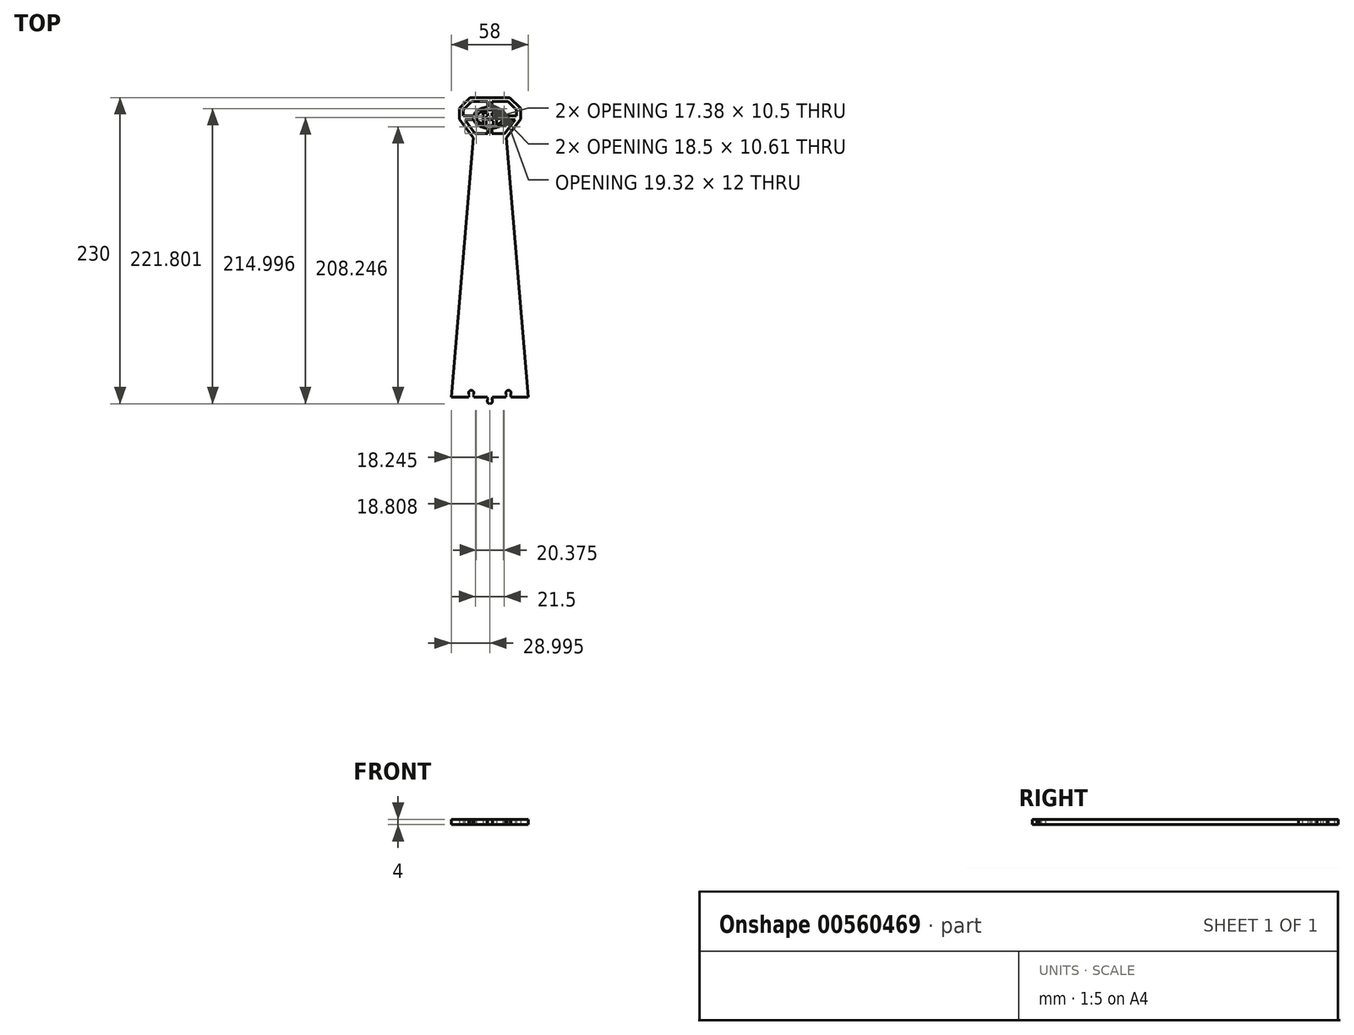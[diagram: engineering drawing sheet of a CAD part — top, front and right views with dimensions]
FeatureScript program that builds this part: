
annotation { "Feature Type Name" : "Feature", "Feature Type Description" : "" }
export const myFeature = defineFeature(function(context is Context, id is Id, definition is map)
    precondition{}
    {
        {
            var Q0;
            Q0=qCreatedBy(makeId("Top.planeOp"),FACE);
            var sketch = newSketch(context, id + "F0", { "sketchPlane" : qUnion([Q0])});
            skLineSegment(sketch, "E0.bottom", {"start": v(14.64, 150.88) * mm, "end": v(-15.36, 150.88) * mm});
            skLineSegment(sketch, "E0.top", {"start": v(12.14, 120.88) * mm, "end": v(-12.86, 120.88) * mm});
            skPoint(sketch, "E0.middle", {"position": v(-0.36, 135.88) * mm});
            skPoint(sketch, "E1", {"position": v(-0.36, 120.88) * mm});
            skPoint(sketch, "E2", {"position": v(-12.86, 120.88) * mm});
            skPoint(sketch, "E3", {"position": v(12.14, 120.88) * mm});
            skLineSegment(sketch, "E4", {"start": v(-15.36, 150.88) * mm, "end": v(-23.36, 142.88) * mm});
            skLineSegment(sketch, "E5", {"start": v(14.64, 150.88) * mm, "end": v(22.64, 142.88) * mm});
            skLineSegment(sketch, "E6", {"start": v(22.64, 142.88) * mm, "end": v(22.64, 134.88) * mm});
            skLineSegment(sketch, "E7", {"start": v(-23.36, 142.88) * mm, "end": v(-23.36, 134.88) * mm});
            skLineSegment(sketch, "E8", {"start": v(-23.36, 134.88) * mm, "end": v(-12.86, 120.88) * mm});
            skLineSegment(sketch, "E9", {"start": v(12.14, 120.88) * mm, "end": v(22.64, 134.88) * mm});
            skPoint(sketch, "E10.orphan", {"position": v(-15.36, 120.88) * mm});
            skEllipticalArc(sketch, "E11", {});
            skEllipticalArc(sketch, "E12", {});
            skLineSegment(sketch, "E13", {"start": v(13.28, 147.99) * mm, "end": v(1.14, 147.99) * mm});
            skLineSegment(sketch, "E14", {"start": v(10.64, 123.88) * mm, "end": v(1.14, 123.88) * mm});
            skLineSegment(sketch, "E15", {"start": v(19.64, 141.63) * mm, "end": v(19.64, 137.38) * mm});
            skLineSegment(sketch, "E16", {"start": v(-11.36, 123.88) * mm, "end": v(-19.24, 134.38) * mm});
            skLineSegment(sketch, "E17", {"start": v(-20.36, 141.63) * mm, "end": v(-20.36, 137.38) * mm});
            skLineSegment(sketch, "E18", {"start": v(-14.01, 147.99) * mm, "end": v(-20.36, 141.63) * mm});
            skLineSegment(sketch, "E19.trimOffspring", {"start": v(19.64, 141.63) * mm, "end": v(13.28, 147.99) * mm});
            skLineSegment(sketch, "E20.trimOffspring", {"start": v(10.64, 123.88) * mm, "end": v(18.51, 134.38) * mm});
            skPoint(sketch, "E21", {"position": v(-0.36, 147.99) * mm});
            skPoint(sketch, "E22", {"position": v(-0.36, 123.88) * mm});
            skPoint(sketch, "E23", {"position": v(-12.86, 135.88) * mm});
            skPoint(sketch, "E24", {"position": v(12.14, 135.88) * mm});
            skLineSegment(sketch, "E25", {"start": v(1.14, 147.99) * mm, "end": v(1.14, 143.82) * mm});
            skLineSegment(sketch, "E26.trimOffspring", {"start": v(1.14, 127.93) * mm, "end": v(1.14, 123.88) * mm});
            skLineSegment(sketch, "E27", {"start": v(-1.86, 147.99) * mm, "end": v(-1.86, 143.82) * mm});
            skLineSegment(sketch, "E28.trimOffspring", {"start": v(-1.86, 127.93) * mm, "end": v(-1.86, 123.88) * mm});
            skLineSegment(sketch, "E29", {"start": v(-20.36, 137.38) * mm, "end": v(-12.64, 137.38) * mm});
            skLineSegment(sketch, "E30", {"start": v(-19.24, 134.38) * mm, "end": v(-12.64, 134.38) * mm});
            skLineSegment(sketch, "E31.trimOffspring", {"start": v(11.91, 134.38) * mm, "end": v(18.51, 134.38) * mm});
            skLineSegment(sketch, "E32.trimOffspring", {"start": v(11.91, 137.38) * mm, "end": v(19.64, 137.38) * mm});
            skLineSegment(sketch, "E33.trimOffspring", {"start": v(-2.86, 137.38) * mm, "end": v(-1.86, 137.38) * mm});
            skPoint(sketch, "E34", {"position": v(-0.36, 137.38) * mm});
            skLineSegment(sketch, "E35", {"start": v(-5.36, 137.38) * mm, "end": v(-5.36, 130.68) * mm});
            skLineSegment(sketch, "E36", {"start": v(4.64, 137.38) * mm, "end": v(4.64, 130.68) * mm});
            skPoint(sketch, "E37.orphan", {"position": v(-10.05, 137.38) * mm});
            skPoint(sketch, "E38.orphan", {"position": v(9.32, 137.38) * mm});
            skLineSegment(sketch, "E39.trimOffspring", {"start": v(1.14, 137.38) * mm, "end": v(2.14, 137.38) * mm});
            skLineSegment(sketch, "E40.trimOffspring", {"start": v(-1.86, 135.38) * mm, "end": v(-1.86, 133.38) * mm});
            skLineSegment(sketch, "E41.trimOffspring", {"start": v(1.14, 135.38) * mm, "end": v(1.14, 133.38) * mm});
            skLineSegment(sketch, "E42", {"start": v(2.14, 135.38) * mm, "end": v(1.14, 135.38) * mm});
            skLineSegment(sketch, "E43", {"start": v(2.14, 133.38) * mm, "end": v(1.14, 133.38) * mm});
            skPoint(sketch, "E44", {"position": v(-0.36, 133.38) * mm});
            skLineSegment(sketch, "E45", {"start": v(-2.86, 133.38) * mm, "end": v(-2.86, 130.07) * mm});
            skLineSegment(sketch, "E46", {"start": v(2.14, 133.38) * mm, "end": v(2.14, 130.07) * mm});
            skLineSegment(sketch, "E47", {"start": v(4.64, 137.38) * mm, "end": v(4.64, 139.38) * mm});
            skLineSegment(sketch, "E48", {"start": v(-5.36, 137.38) * mm, "end": v(-5.36, 139.38) * mm});
            skLineSegment(sketch, "E49", {"start": v(4.64, 139.38) * mm, "end": v(1.14, 139.38) * mm});
            skLineSegment(sketch, "E50", {"start": v(-1.86, 137.38) * mm, "end": v(-1.86, 139.38) * mm});
            skLineSegment(sketch, "E51", {"start": v(1.14, 137.38) * mm, "end": v(1.14, 139.38) * mm});
            skLineSegment(sketch, "E52", {"start": v(2.14, 135.38) * mm, "end": v(2.14, 137.38) * mm});
            skLineSegment(sketch, "E53", {"start": v(-2.86, 135.38) * mm, "end": v(-2.86, 137.38) * mm});
            skLineSegment(sketch, "E54.trimOffspring", {"start": v(-1.86, 139.38) * mm, "end": v(-5.36, 139.38) * mm});
            skLineSegment(sketch, "E55.trimOffspring", {"start": v(-1.86, 135.38) * mm, "end": v(-2.86, 135.38) * mm});
            skLineSegment(sketch, "E56.trimOffspring", {"start": v(-1.86, 133.38) * mm, "end": v(-2.86, 133.38) * mm});
            skPoint(sketch, "E57.orphan", {"position": v(-5.36, 133.38) * mm});
            skPoint(sketch, "E58.orphan", {"position": v(4.64, 133.38) * mm});
            skEllipticalArc(sketch, "E59.trimOffspring", {});
            skLineSegment(sketch, "E60.trimOffspring", {"start": v(-1.86, 123.88) * mm, "end": v(-11.36, 123.88) * mm});
            skEllipticalArc(sketch, "E61.trimOffspring", {});
            skEllipticalArc(sketch, "E62.trimOffspring", {});
            skEllipticalArc(sketch, "E63.trimOffspring", {});
            skLineSegment(sketch, "E64.trimOffspring", {"start": v(-1.86, 147.99) * mm, "end": v(-14.01, 147.99) * mm});
            skLineSegment(sketch, "E65.bottom", {"start": v(-12.86, 120.88) * mm, "end": v(12.14, 120.88) * mm});
            skPoint(sketch, "E66", {"position": v(-0.36, -74.12) * mm});
            skLineSegment(sketch, "E67", {"start": v(28.64, -74.12) * mm, "end": v(15.64, -74.12) * mm});
            skLineSegment(sketch, "E68", {"start": v(-29.36, -74.12) * mm, "end": v(-12.86, 120.88) * mm});
            skLineSegment(sketch, "E69", {"start": v(28.64, -74.12) * mm, "end": v(12.14, 120.88) * mm});
            skPoint(sketch, "E70", {"position": v(-14.36, -74.12) * mm});
            skPoint(sketch, "E71", {"position": v(13.64, -74.12) * mm});
            skLineSegment(sketch, "E72", {"start": v(-16.36, -74.12) * mm, "end": v(-16.36, -73.12) * mm});
            skLineSegment(sketch, "E73", {"start": v(-12.36, -74.12) * mm, "end": v(-12.36, -73.12) * mm});
            skLineSegment(sketch, "E74", {"start": v(15.64, -74.12) * mm, "end": v(15.64, -73.12) * mm});
            skLineSegment(sketch, "E75", {"start": v(11.64, -74.12) * mm, "end": v(11.64, -73.12) * mm});
            skPoint(sketch, "E76", {"position": v(-14.36, -71.12) * mm});
            skPoint(sketch, "E77", {"position": v(13.64, -71.12) * mm});
            skArc(sketch, "E78", {"start": v(-12.95, -72.54) * mm, "mid": v(-14.36, -69.12) * mm, "end": v(-15.78, -72.54) * mm});
            skArc(sketch, "E79", {"start": v(15.05, -72.54) * mm, "mid": v(13.64, -69.12) * mm, "end": v(12.22, -72.54) * mm});
            skLineSegment(sketch, "E80", {"start": v(11.64, -73.12) * mm, "end": v(12.22, -72.54) * mm});
            skLineSegment(sketch, "E81", {"start": v(15.64, -73.12) * mm, "end": v(15.05, -72.54) * mm});
            skLineSegment(sketch, "E82", {"start": v(-12.36, -73.12) * mm, "end": v(-12.95, -72.54) * mm});
            skLineSegment(sketch, "E83", {"start": v(-16.36, -73.12) * mm, "end": v(-15.78, -72.54) * mm});
            skArc(sketch, "E84", {"start": v(-1.78, -75.71) * mm, "mid": v(-0.36, -79.12) * mm, "end": v(1.05, -75.71) * mm});
            skLineSegment(sketch, "E85", {"start": v(-2.36, -74.12) * mm, "end": v(-2.36, -75.12) * mm});
            skLineSegment(sketch, "E86", {"start": v(1.64, -74.12) * mm, "end": v(1.64, -75.12) * mm});
            skLineSegment(sketch, "E87", {"start": v(-2.36, -75.12) * mm, "end": v(-1.78, -75.71) * mm});
            skLineSegment(sketch, "E88", {"start": v(1.64, -75.12) * mm, "end": v(1.05, -75.71) * mm});
            skPoint(sketch, "E89.orphan", {"position": v(-2.36, -79.12) * mm});
            skPoint(sketch, "E90.trimOffspring.end.orphan", {"position": v(-0.36, -79.12) * mm});
            skLineSegment(sketch, "E91.trimOffspring", {"start": v(-2.36, -74.12) * mm, "end": v(-12.36, -74.12) * mm});
            skLineSegment(sketch, "E92.trimOffspring", {"start": v(-16.36, -74.12) * mm, "end": v(-29.36, -74.12) * mm});
            skPoint(sketch, "E93.orphan", {"position": v(-12.36, -71.12) * mm});
            skPoint(sketch, "E94.trimOffspring.end.orphan", {"position": v(-16.36, -71.12) * mm});
            skLineSegment(sketch, "E95.trimOffspring", {"start": v(11.64, -74.12) * mm, "end": v(1.64, -74.12) * mm});
            skPoint(sketch, "E96.orphan", {"position": v(11.64, -71.12) * mm});
            skPoint(sketch, "E97.start.orphan", {"position": v(15.64, -71.12) * mm});
            const initialGuessF0  = {"E11": [-0.0003648042464688972, 0.13587578032428296, 1, 0, 0.0125, 0.008, 4.832678862779479, 6.094568921004184], "E12": [-0.0003648042464688972, 0.13587578032428296, 1, 0, 0.01, 0.006, 5.235987755982989, 4.188790204786391], "E59.trimOffspring": [-0.0003648042464688972, 0.13587578032428296, 1, 0, 0.01, 0.006, 4.459708725242612, 4.9650692355267685], "E61.trimOffspring": [-0.0003648042464688972, 0.13587578032428296, 1, 0, 0.0125, 0.008, 1.6910862091896828, 2.952976267414389], "E62.trimOffspring": [-0.0003648042464688972, 0.13587578032428296, 1, 0, 0.0125, 0.008, 0.18861638617540466, 1.4505064444001077], "E63.trimOffspring": [-0.0003648042464688972, 0.13587578032428296, 1, 0, 0.0125, 0.008, 3.330209039765196, 4.592099097989903]};
            skSetInitialGuess(sketch, initialGuessF0);
            skSolve(sketch);
        }
        {
            var Q0;
            Q0=qSketchRegion(id+"F0",true);
            extrude(context, id + "F1", {"entities" : qUnion([Q0]), "depth" : 4 * mm, "offsetDistance" : 25 * mm});
        }
    });
